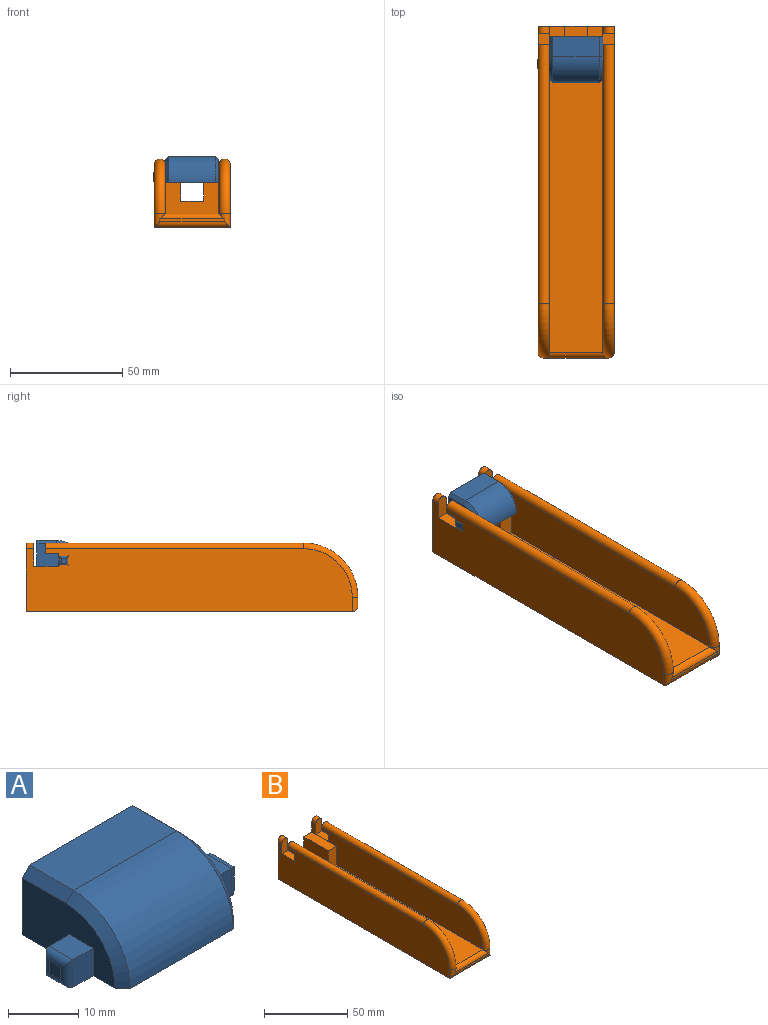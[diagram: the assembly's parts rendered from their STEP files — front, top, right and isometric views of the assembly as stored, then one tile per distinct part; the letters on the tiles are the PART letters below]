
ASSEMBLY  parts=2 mates=1
PART A: 26 faces, bbox 34.5x20.3x11.4 mm
  f0: plane 18.8x9.91mm, normal (-1,0,0), area 141.8mm2, adj f2,f4,f5,f6,f7,f14,f15
  f1: plane 18.8x9.91mm, normal (1,0,0), area 141.8mm2, adj f2,f4,f9,f10,f11,f16,f17
  f2: plane 23.88x11.43mm, normal (0,1,0), area 270.6mm2, adj f0,f1,f3,f4,f14,f17
  f3: plane 20.83x8.89mm, normal (0,0,1), area 185.2mm2, adj f2,f13,f14,f17
  f4: plane 32x20.32mm, normal (0,0,-1), area 522.1mm2, adj f0,f1,f2,f5,f7,f9,f11,f13
  f5: plane 4.83x4.06mm, normal (0,-1,0), area 19.6mm2, adj f0,f4,f6,f23
  f6: plane 4.83x4.06mm, normal (0,0,1), area 19.6mm2, adj f0,f5,f7,f25
  f7: plane 4.83x4.06mm, normal (0,1,0), area 19.6mm2, adj f0,f4,f6,f24
  f8: plane 2.29x2.29mm, normal (-1,0,0), area 5.2mm2, adj f22,f23,f24,f25
  f9: plane 4.83x4.06mm, normal (0,1,0), area 19.6mm2, adj f1,f4,f10,f20
  f10: plane 4.83x4.06mm, normal (0,0,1), area 19.6mm2, adj f1,f9,f11,f21
  f11: plane 4.83x4.06mm, normal (0,-1,0), area 19.6mm2, adj f1,f4,f10,f19
  f12: plane 2.29x2.29mm, normal (1,0,0), area 5.2mm2, adj f18,f19,f20,f21
  f13: cylinder r=11.43mm len=20.83mm, axis (-1,0,0), area 374mm2, adj f3,f4,f15,f16
  f14: plane 8.89x1.52mm, normal (-0.71,0,0.71), area 19.2mm2, adj f0,f2,f3,f15
  f15: cone r=9.91mm half-angle=45deg, axis (1,0,0), area 36.1mm2, adj f0,f4,f13,f14
  f16: cone r=9.91mm half-angle=45deg, axis (-1,0,0), area 36.1mm2, adj f1,f4,f13,f17
  f17: plane 8.89x1.52mm, normal (0.71,0,0.71), area 19.2mm2, adj f1,f2,f3,f16
  f18: cylinder r=1.27mm len=4.83mm, axis (0,-1,0), area 7.8mm2, adj f4,f12,f19,f20
  f19: cylinder r=1.27mm len=4.83mm, axis (0,0,1), area 7.8mm2, adj f11,f12,f18,f21
  f20: cylinder r=1.27mm len=4.83mm, axis (0,0,-1), area 7.8mm2, adj f9,f12,f18,f21
  f21: cylinder r=1.27mm len=4.83mm, axis (0,1,0), area 7.8mm2, adj f10,f12,f19,f20
  f22: cylinder r=1.27mm len=4.83mm, axis (0,-1,0), area 7.8mm2, adj f4,f8,f23,f24
  f23: cylinder r=1.27mm len=4.83mm, axis (0,0,-1), area 7.8mm2, adj f5,f8,f22,f25
  f24: cylinder r=1.27mm len=4.83mm, axis (0,0,1), area 7.8mm2, adj f7,f8,f22,f25
  f25: cylinder r=1.27mm len=4.83mm, axis (0,-1,0), area 7.8mm2, adj f6,f8,f23,f24
PART B: 34 faces, bbox 33.9x149.6x32.5 mm
  f0: plane 145.03x27.94mm, normal (1,0,0), area 3880.5mm2, adj f5,f8,f14,f15,f16,f17,f18,f24
  f1: plane 145.03x27.94mm, normal (-1,0,0), area 3880.5mm2, adj f5,f8,f19,f20,f21,f22,f23,f29
  f2: plane 145.03x21.59mm, normal (1,0,0), area 2677.4mm2, adj f5,f6,f9,f10,f19,f20,f21,f22
  f3: plane 145.03x21.59mm, normal (-1,0,0), area 2677.4mm2, adj f4,f5,f6,f9,f14,f15,f16,f17
  f4: plane 20.57x6.79mm, normal (0,0,1), area 139.8mm2, adj f3,f5,f9,f11
  f5: plane 33.91x30.48mm, normal (0,1,0), area 695.5mm2, adj f0,f1,f2,f3,f4,f8,f10,f11
  f6: plane 124.46x23.75mm, normal (0,0,1), area 2955.8mm2, adj f2,f3,f9,f28
  f7: plane 28.83x1.27mm, normal (0,-1,0), area 36.6mm2, adj f26,f27,f28,f29
  f8: plane 145.03x33.91mm, normal (0,0,-1), area 4918mm2, adj f0,f1,f5,f27
  f9: plane 23.75x13.72mm, normal (0,-1,0), area 240.6mm2, adj f2,f3,f4,f6,f10,f11,f12,f13
  f10: plane 20.57x6.79mm, normal (0,0,1), area 139.8mm2, adj f2,f5,f9,f12
  f11: plane 20.57x8.38mm, normal (-1,0,0), area 172.5mm2, adj f4,f5,f9,f13
  f12: plane 20.57x8.38mm, normal (1,0,0), area 172.5mm2, adj f5,f9,f10,f13
  f13: plane 20.57x10.16mm, normal (0,0,1), area 209mm2, adj f5,f9,f11,f12
  f14: plane 5.08x4.83mm, normal (0,1,0), area 21.8mm2, adj f0,f3,f18,f24
  f15: plane 5.46x5.08mm, normal (0,1,0), area 27.7mm2, adj f0,f3,f16,f18
  f16: plane 10.99x5.08mm, normal (0,0,1), area 55.8mm2, adj f0,f3,f15,f17
  f17: plane 10.29x5.08mm, normal (0,-1,0), area 49.5mm2, adj f0,f3,f16,f32
  f18: plane 5.91x5.08mm, normal (0,0,-1), area 30mm2, adj f0,f3,f14,f15
  f19: plane 5.91x5.08mm, normal (0,0,-1), area 30mm2, adj f1,f2,f20,f23
  f20: plane 5.08x4.83mm, normal (0,1,0), area 21.8mm2, adj f1,f2,f19,f31
  f21: plane 10.29x5.08mm, normal (0,-1,0), area 49.5mm2, adj f1,f2,f22,f33
  f22: plane 10.99x5.08mm, normal (0,0,1), area 55.8mm2, adj f1,f2,f21,f23
  f23: plane 5.46x5.08mm, normal (0,1,0), area 27.7mm2, adj f1,f2,f19,f22
  f24: cylinder r=2.54mm len=115mm, axis (0,1,0), area 917.6mm2, adj f0,f3,f14,f25
  f25: torus R=21.59mm, axis (1,0,0), area 290.9mm2, adj f0,f3,f24,f26
  f26: cylinder r=2.54mm len=6.35mm, axis (0,0,-1), area 25.3mm2, adj f0,f7,f25,f27,f28
  f27: cylinder r=2.54mm len=33.91mm, axis (-1,0,0), area 127.9mm2, adj f7,f8,f26,f29
  f28: cylinder r=2.54mm len=28.83mm, axis (1,0,0), area 102.1mm2, adj f6,f7,f26,f29
  f29: cylinder r=2.54mm len=6.35mm, axis (0,0,1), area 25.3mm2, adj f1,f7,f27,f28,f30
  f30: torus R=21.59mm, axis (1,0,0), area 290.9mm2, adj f1,f2,f29,f31
  f31: cylinder r=2.54mm len=115mm, axis (0,-1,0), area 917.6mm2, adj f1,f2,f20,f30
  f32: cylinder r=2.54mm len=5.08mm, axis (0,1,0), area 26.9mm2, adj f0,f3,f5,f17
  f33: cylinder r=2.54mm len=5.08mm, axis (0,-1,0), area 26.9mm2, adj f1,f2,f5,f21
PLACE A t=(-42.16,1,32.29)mm
PLACE B t=(-42.19,-69.82,18.46)mm
MATE fastened B.f3 <-> A.f1  axis (-1,0,0) through (-30.22,1.63,32.29)mm
